# Revit family: Sanitary_Accessories_DURAVIT-AG_DuraStyle-Siphon-cover-085831
name_source: partatom
category: Specialty Equipment
revit_build: Autodesk Revit 2018 (Build: 20180329_1100(x64)
units: mm (PartAtom-declared; Revit-internal decimal feet)

## family parameters
Cut with Voids When Loaded = No
Host = Face
OmniClass Number = 23.19.31.17
OmniClass Title = Sanitary Room Units
Part Type = Normal
Room Calculation Point = No
Round Connector Dimension = Use Diameter
Shared = No

## types (2) — shared parameters
BIMobject category = Bathroom Accessories
Default Elevation = 1219 mm
Design country = Germany
ETIM classification = EC011331 | Siphon cover
Edition number = 1
IFC Classification = Furnishing Element
Installation instructions = https://pro.duravit.com
Manufacturer = Duravit
Manufacturer country = Germany
Manufacturer name = DURAVIT AG
Masterformat 2014 Code = 01 52 19
Masterformat 2014 Description = Sanitary Facilities
Material main = Ceramics
Model = DuraStyle Siphon cover - 085831
OmniClass Code = 23-19 31 17
OmniClass Description = Sanitary Room Units
Product Guid = 8ce1898f-7e09-4aab-88f4-b3c17c87b010
Product SKU = DuraStyle-Siphon-cover-085831
Product certification = https://pro.duravit.com
Product data url = https://bimobject.com
Product family = DuraStyle
Product group = Siphon cover
Product name = DuraStyle Siphon cover - 085831
Product url = https://pro.duravit.com
QR code = https://bimobject.com
Technical description = https://pro.duravit.com
UNSPSC Code = 301815
URL = https://www.duravit.com
Uniclass 2015 Code = Pr_40_20
Uniclass 2015 Name = Sanitary fittings and accessories
Uniformat II Code = D2010
Uniformat II Description = Plumbing Fixtures
Weight Net (Kg) = 5.4
Youtube clip = https://pro.duravit.com

## per-type parameters (varying)
| type | Description | Main material |
| 00 - White Alpin WonderGliss | Duravit DuraStyle Siphon cover White High Gloss , WonderGliss - 08583100001 | Duravit - Ceramic - 00 - White Alpin WonderGliss |
| 00 - White Alpin | Duravit DuraStyle Siphon cover White High Gloss - 0858310000 | Duravit - Ceramic - 00 - White Alpin |

## geometry (parser evidence)
native form markers: Sweep x3
no freeform markers — native parametric forms only
